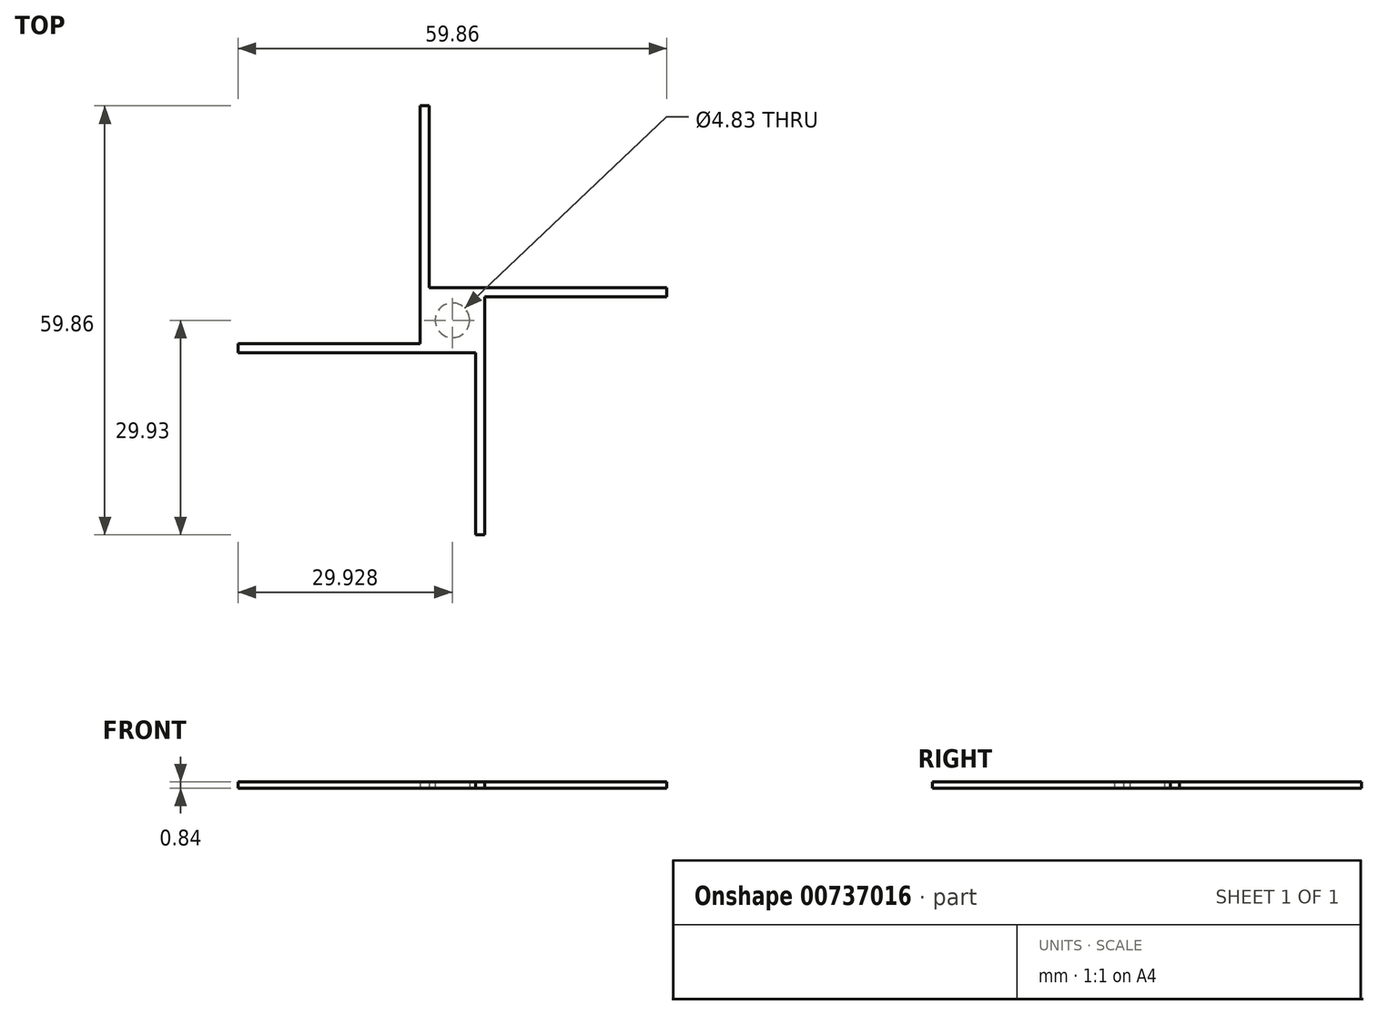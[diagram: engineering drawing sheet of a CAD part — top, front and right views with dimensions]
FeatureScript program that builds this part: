
annotation { "Feature Type Name" : "Feature", "Feature Type Description" : "" }
export const myFeature = defineFeature(function(context is Context, id is Id, definition is map)
    precondition{}
    {
        {
            assignVariable(context, id + "F0", {"name" : "BaseHeight", "anyValue" : 0.04});
        }
        {
            assignVariable(context, id + "F1", {"name" : "PoleRadius", "anyValue" : 0.07});
        }
        {
            assignVariable(context, id + "F2", {"name" : "PoleHeight", "anyValue" : 0.75});
        }
        {
            assignVariable(context, id + "F3", {"name" : "ConeHeight", "anyValue" : 0.1});
        }
        {
            assignVariable(context, id + "F4", {"name" : "PoleClearance", "anyValue" : 0.02});
        }
        {
            assignVariable(context, id + "F5", {"name" : "BladeBaseClearance", "anyValue" : 0.03});
        }
        {
            var Q0;
            Q0=qCreatedBy(makeId("Top.planeOp"),FACE);
            var sketch = newSketch(context, id + "F6", { "sketchPlane" : qUnion([Q0])});
            skLineSegment(sketch, "E0.bottom", {"start": v(-92.43, -23.92) * mm, "end": v(-100.22, -23.92) * mm});
            skLineSegment(sketch, "E0.top", {"start": v(-91.16, -14.86) * mm, "end": v(-98.95, -14.86) * mm});
            skLineSegment(sketch, "E0.left", {"start": v(-91.16, -23.92) * mm, "end": v(-91.16, -16.13) * mm});
            skLineSegment(sketch, "E0.right", {"start": v(-100.22, -22.65) * mm, "end": v(-100.22, -14.86) * mm});
            skPoint(sketch, "E0.middle", {"position": v(-95.7, -19.4) * mm});
            skLineSegment(sketch, "E1.bottom", {"start": v(-91.16, -14.86) * mm, "end": v(-93.28, -14.86) * mm});
            skLineSegment(sketch, "E1.top", {"start": v(-91.16, -49.32) * mm, "end": v(-92.43, -49.32) * mm});
            skLineSegment(sketch, "E1.left", {"start": v(-91.16, -23.92) * mm, "end": v(-91.16, -49.32) * mm});
            skLineSegment(sketch, "E2.bottom", {"start": v(-92.43, -23.92) * mm, "end": v(-125.62, -23.92) * mm});
            skLineSegment(sketch, "E2.right", {"start": v(-125.62, -23.92) * mm, "end": v(-125.62, -22.65) * mm});
            skLineSegment(sketch, "E3.top", {"start": v(-100.22, 10.54) * mm, "end": v(-98.95, 10.54) * mm});
            skLineSegment(sketch, "E3.left", {"start": v(-100.22, -22.65) * mm, "end": v(-100.22, 10.54) * mm});
            skLineSegment(sketch, "E4.bottom", {"start": v(-98.95, -14.86) * mm, "end": v(-65.76, -14.86) * mm});
            skLineSegment(sketch, "E4.right", {"start": v(-65.76, -14.86) * mm, "end": v(-65.76, -16.13) * mm});
            skLineSegment(sketch, "E5.trimOffspring", {"start": v(-91.16, -16.13) * mm, "end": v(-65.76, -16.13) * mm});
            skLineSegment(sketch, "E6.trimOffspring", {"start": v(-100.22, -22.65) * mm, "end": v(-125.62, -22.65) * mm});
            skLineSegment(sketch, "E7.trimOffspring", {"start": v(-98.95, -14.86) * mm, "end": v(-98.95, 10.54) * mm});
            skLineSegment(sketch, "E8.trimOffspring", {"start": v(-92.43, -23.92) * mm, "end": v(-92.43, -49.32) * mm});
            skSolve(sketch);
        }
        {
            var Q0;
            Q0=makeQuery(id+"F6.imprint","IMPRINT",FACE,{"disambiguationData":[TD([[makeQuery(id+"F6.imprint","IMPRINT",EDGE,{"derivedFrom":sQuery(id+"F6.wireOp",EDGE,"E0.bottom")}),-1.0]])]});
            var Q1;
            Q1=makeQuery(id+"F6.imprint","IMPRINT",FACE,{"disambiguationData":[TD([[makeQuery(id+"F6.imprint","IMPRINT",EDGE,{"derivedFrom":sQuery(id+"F6.wireOp",EDGE,"E0.left")}),1.0]])]});
            extrude(context, id + "F7", {"entities" : qUnion([Q0, Q1]), "depth" : (((getVariable(context, 'PoleHeight') + getVariable(context, 'ConeHeight')) - (getVariable(context, 'BaseHeight') + getVariable(context, 'BladeBaseClearance'))) + 0.05) * mm, "offsetDistance" : 25.4 * mm});
        }
        {
            var Q0;
            Q0=makeQuery(id+"F7.opExtrude","CAP_FACE",FACE,{"disambiguationData":[OSD([sQuery(id+"F6.wireOp",EDGE,"E0.bottom"),sQuery(id+"F6.wireOp",EDGE,"E0.top"),sQuery(id+"F6.wireOp",EDGE,"E0.left"),sQuery(id+"F6.wireOp",EDGE,"E0.right")])],"isStart":true});
            var sketch = newSketch(context, id + "F8", { "sketchPlane" : qUnion([Q0])});
            skCircle(sketch, "E9", {"center": v(-95.7, 19.4) * mm, "radius": 2.41 * mm});
            skSolve(sketch);
        }
        {
            var Q0;
            Q0=makeQuery(id+"F8.imprint","IMPRINT",FACE,{"disambiguationData":[TD([[makeQuery(id+"F8.imprint","IMPRINT",EDGE,{"derivedFrom":sQuery(id+"F8.wireOp",EDGE,"E9")}),1.0]])]});
            extrude(context, id + "F9", {"entities" : qUnion([Q0]), "operationType" : NewBodyOperationType.REMOVE, "oppositeDirection" : true, "depth" : (((getVariable(context, 'PoleHeight') + getVariable(context, 'ConeHeight')) - (getVariable(context, 'BaseHeight') + getVariable(context, 'BladeBaseClearance')))) * mm, "offsetDistance" : 25.4 * mm});
        }
        {
            var Q0;
            Q0=makeQuery(id+"F9.boolean.opBoolean","COPY",FACE,{"derivedFrom":makeQuery(id+"F9.opExtrude","CAP_FACE",FACE,{"disambiguationData":[OSD([sQuery(id+"F8.wireOp",EDGE,"E9")])],"isStart":false})});
            fillet(context, id + "F10", {"entities" : qUnion([Q0]), "radius" : (getVariable(context, 'PoleRadius') + getVariable(context, 'PoleClearance')) * mm, "tangentPropagation" : true, "allowEdgeOverflow" : false});
        }
    });
